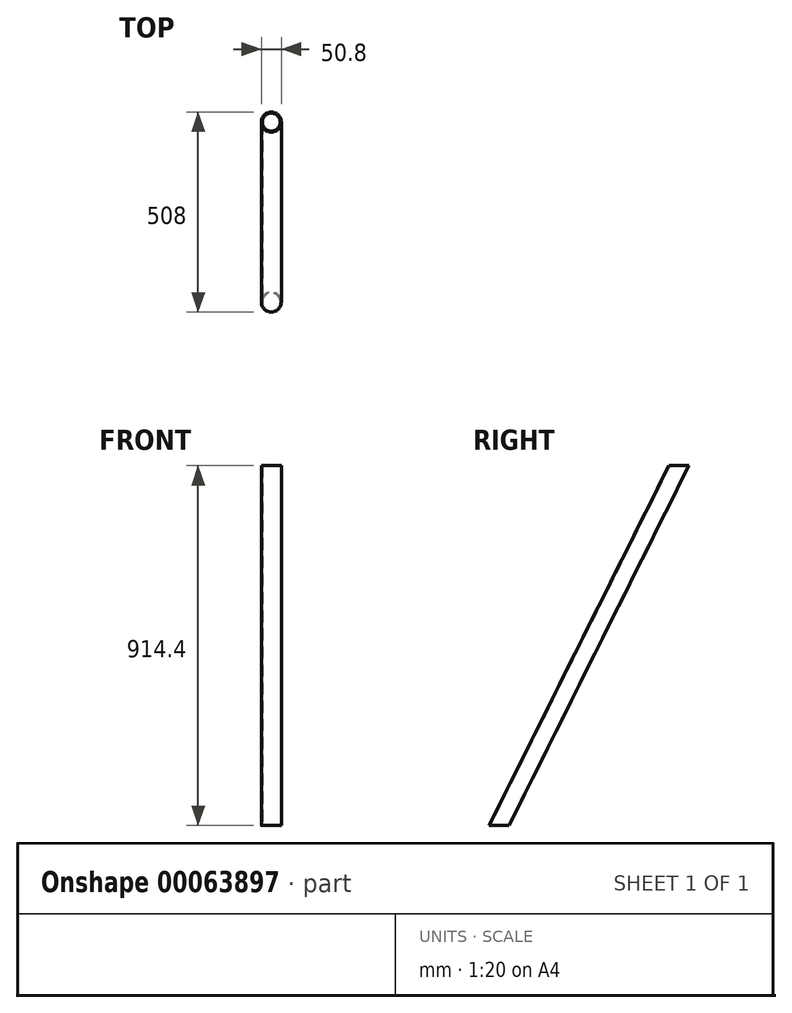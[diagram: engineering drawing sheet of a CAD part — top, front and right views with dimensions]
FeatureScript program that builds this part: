
annotation { "Feature Type Name" : "Feature", "Feature Type Description" : "" }
export const myFeature = defineFeature(function(context is Context, id is Id, definition is map)
    precondition{}
    {
        {
            var Q0;
            Q0=qCreatedBy(makeId("Top.planeOp"),FACE);
            var sketch = newSketch(context, id + "F0", { "sketchPlane" : qUnion([Q0])});
            skCircle(sketch, "E0", {"center": v(0, 0) * mm, "radius": 25.4 * mm});
            skCircle(sketch, "E1", {"center": v(0, 0) * mm, "radius": 22.86 * mm});
            skSolve(sketch);
        }
        {
            var Q0;
            Q0=qCreatedBy(makeId("Right.planeOp"),FACE);
            var sketch = newSketch(context, id + "F1", { "sketchPlane" : qUnion([Q0])});
            skLineSegment(sketch, "E2", {"start": v(0, 0) * mm, "end": v(0, 914.4) * mm, "construction": true});
            skLineSegment(sketch, "E3", {"start": v(0, 0) * mm, "end": v(457.2, 914.4) * mm});
            skLineSegment(sketch, "E4", {"start": v(0, 914.4) * mm, "end": v(457.2, 914.4) * mm, "construction": true});
            skSolve(sketch);
        }
        {
            var Q0;
            Q0=makeQuery(id+"F0.imprint","IMPRINT",FACE,{"disambiguationData":[TD([[makeQuery(id+"F0.imprint","IMPRINT",EDGE,{"derivedFrom":sQuery(id+"F0.wireOp",EDGE,"E0")}),1.0]])]});
            var Q1;
            Q1=sQuery(id+"F0.wireOp",EDGE,"E0");
            var Q2;
            Q2=sQuery(id+"F1.wireOp",EDGE,"E3");
            sweep(context, id + "F2", {"profiles" : qUnion([Q0]), "surfaceProfiles" : qUnion([Q1]), "path" : qUnion([Q2])});
        }
    });
